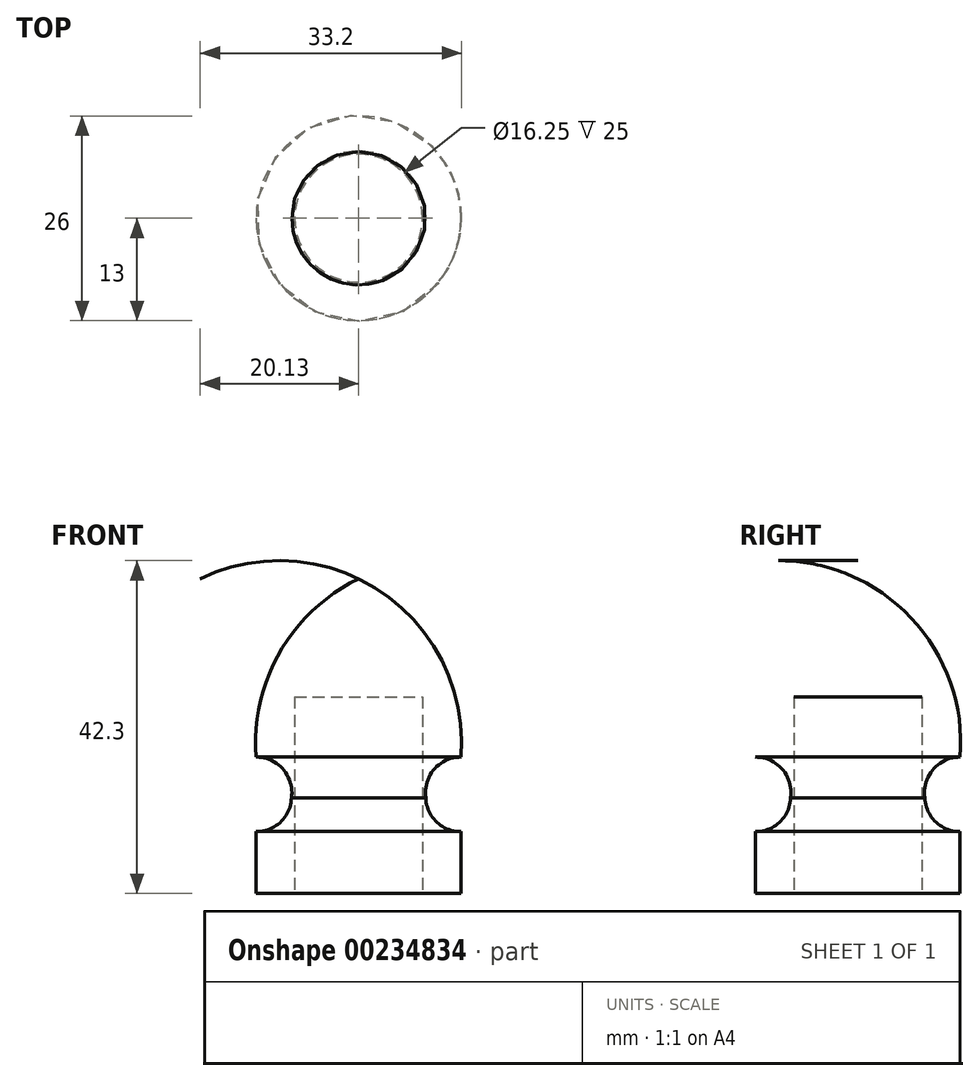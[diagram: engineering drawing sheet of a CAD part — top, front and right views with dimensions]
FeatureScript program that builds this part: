
annotation { "Feature Type Name" : "Feature", "Feature Type Description" : "" }
export const myFeature = defineFeature(function(context is Context, id is Id, definition is map)
    precondition{}
    {
        {
            var Q0;
            Q0=qCreatedBy(makeId("Front.planeOp"),FACE);
            var sketch = newSketch(context, id + "F0", { "sketchPlane" : qUnion([Q0])});
            skLineSegment(sketch, "E0", {"start": v(0, 0) * mm, "end": v(0, 40) * mm});
            skArc(sketch, "E1", {"start": v(0, 40) * mm, "mid": v(-10, 30.68) * mm, "end": v(-13, 17.35) * mm});
            skArc(sketch, "E2", {"start": v(-8.53, 12.15) * mm, "mid": v(-9.57, 15.77) * mm, "end": v(-13, 17.35) * mm});
            skArc(sketch, "E3", {"start": v(-13, 7.88) * mm, "mid": v(-9.9, 9.1) * mm, "end": v(-8.53, 12.15) * mm});
            skLineSegment(sketch, "E4", {"start": v(-13, 7.88) * mm, "end": v(-13, 0) * mm});
            skLineSegment(sketch, "E5", {"start": v(-13, 0) * mm, "end": v(0, 0) * mm});
            skPoint(sketch, "E6.end.orphan", {"position": v(0, 17.35) * mm});
            skSolve(sketch);
        }
        {
            var Q0;
            Q0 = qSketchRegion(id + "F0", true);
            var Q1;
            Q1=sQuery(id+"F0.wireOp",EDGE,"E0");
            revolve(context, id + "F1", {"entities" : qUnion([Q0]), "axis" : qUnion([Q1]), "revolveType" : RevolveType.FULL});
        }
        {
            var Q0;
            Q0=makeQuery(id+"F1.opRevolve","SWEPT_FACE",FACE,{"disambiguationData":[OSD([sQuery(id+"F0.wireOp",EDGE,"E5")])]});
            var sketch = newSketch(context, id + "F2", { "sketchPlane" : qUnion([Q0])});
            skCircle(sketch, "E7", {"center": v(0, 0) * mm, "radius": 8.12 * mm});
            skSolve(sketch);
        }
        {
            var Q0;
            Q0 = qSketchRegion(id + "F2", true);
            extrude(context, id + "F3", {"entities" : qUnion([Q0]), "operationType" : NewBodyOperationType.REMOVE, "oppositeDirection" : true, "depth" : 25 * mm});
        }
    });
